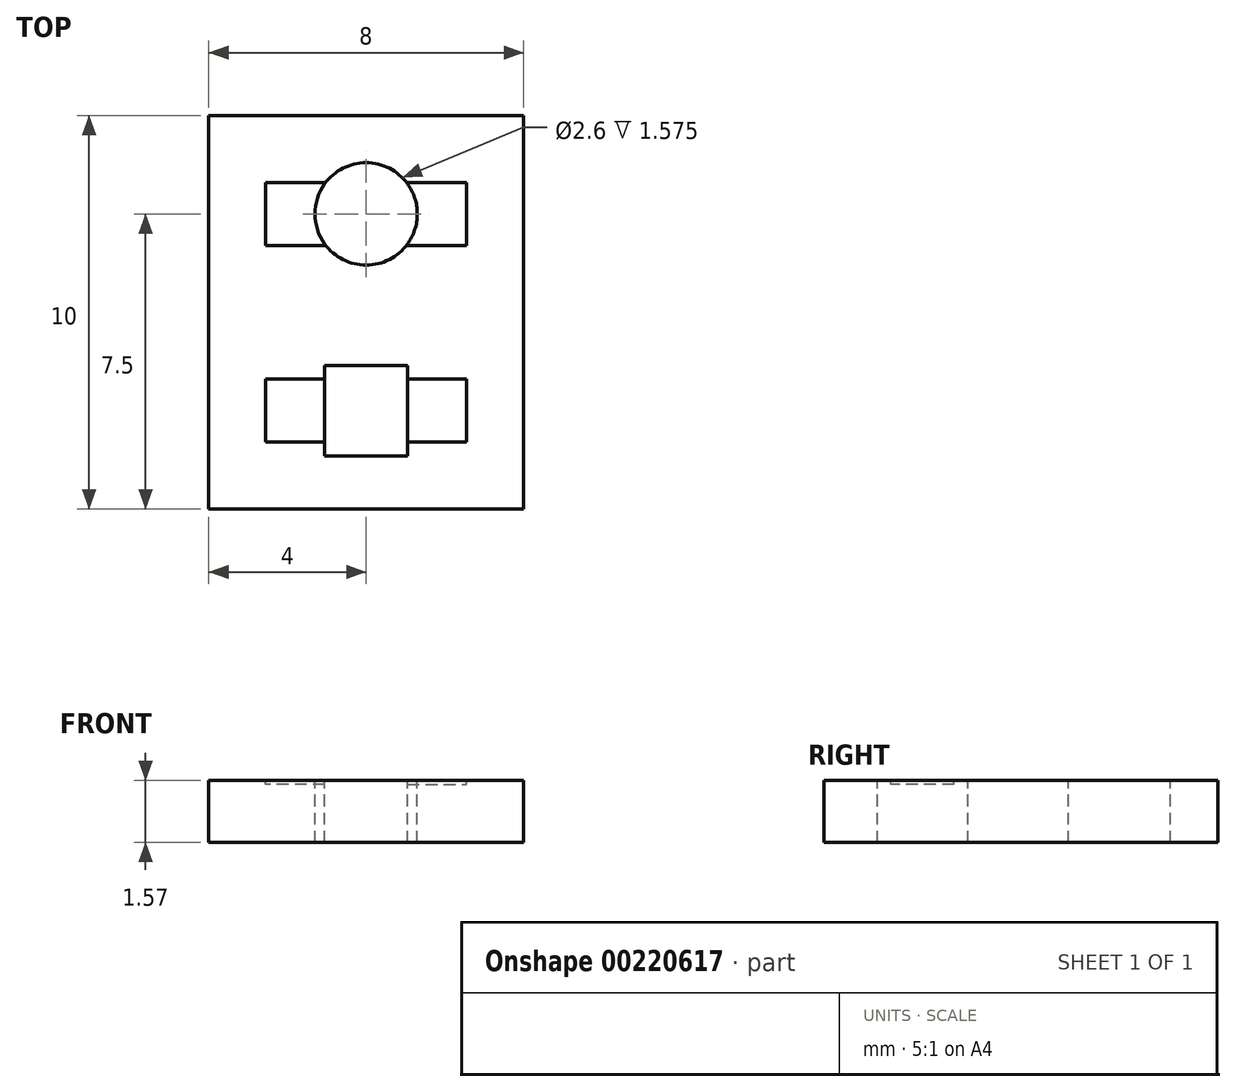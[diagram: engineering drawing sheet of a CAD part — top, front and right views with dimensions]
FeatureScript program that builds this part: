
annotation { "Feature Type Name" : "Feature", "Feature Type Description" : "" }
export const myFeature = defineFeature(function(context is Context, id is Id, definition is map)
    precondition{}
    {
        {
            var Q0;
            Q0=qCreatedBy(makeId("Top.planeOp"),FACE);
            var sketch = newSketch(context, id + "F0", { "sketchPlane" : qUnion([Q0])});
            skLineSegment(sketch, "E0.bottom", {"start": v(4, 2.5) * mm, "end": v(-4, 2.5) * mm});
            skLineSegment(sketch, "E0.top", {"start": v(4, -2.5) * mm, "end": v(-4, -2.5) * mm});
            skLineSegment(sketch, "E0.left", {"start": v(4, 2.5) * mm, "end": v(4, -2.5) * mm});
            skLineSegment(sketch, "E0.right", {"start": v(-4, 2.5) * mm, "end": v(-4, -2.5) * mm});
            skPoint(sketch, "E0.middle", {"position": v(0, 0) * mm});
            skLineSegment(sketch, "E1.bottom", {"start": v(1.05, 1.15) * mm, "end": v(-1.05, 1.15) * mm});
            skLineSegment(sketch, "E1.top", {"start": v(1.05, -1.15) * mm, "end": v(-1.05, -1.15) * mm});
            skLineSegment(sketch, "E1.left", {"start": v(1.05, 1.15) * mm, "end": v(1.05, -1.15) * mm});
            skLineSegment(sketch, "E1.right", {"start": v(-1.05, 1.15) * mm, "end": v(-1.05, -1.15) * mm});
            skLineSegment(sketch, "E2.bottom", {"start": v(-1.05, 0.8) * mm, "end": v(-2.55, 0.8) * mm});
            skLineSegment(sketch, "E2.top", {"start": v(-1.05, -0.8) * mm, "end": v(-2.55, -0.8) * mm});
            skLineSegment(sketch, "E2.left", {"start": v(-1.05, 0.8) * mm, "end": v(-1.05, -0.8) * mm});
            skLineSegment(sketch, "E2.right", {"start": v(-2.55, 0.8) * mm, "end": v(-2.55, -0.8) * mm});
            skLineSegment(sketch, "E3.bottom", {"start": v(1.05, -0.8) * mm, "end": v(2.55, -0.8) * mm});
            skLineSegment(sketch, "E3.top", {"start": v(1.05, 0.8) * mm, "end": v(2.55, 0.8) * mm});
            skLineSegment(sketch, "E3.left", {"start": v(1.05, 0.8) * mm, "end": v(1.05, -0.8) * mm});
            skLineSegment(sketch, "E3.right", {"start": v(2.55, 0.8) * mm, "end": v(2.55, -0.8) * mm});
            skLineSegment(sketch, "E4", {"start": v(-1.05, 0) * mm, "end": v(0, 0) * mm, "construction": true});
            skLineSegment(sketch, "E5", {"start": v(0, 0) * mm, "end": v(1.05, 0) * mm, "construction": true});
            skLineSegment(sketch, "E6", {"start": v(-1.8, 0.8) * mm, "end": v(-1.8, -0.8) * mm, "construction": true});
            skSolve(sketch);
        }
        {
            var Q0;
            Q0 = qSketchRegion(id + "F0", true);
            var Q1;
            Q1=makeQuery(id+"F0.imprint","IMPRINT",FACE,{"disambiguationData":[TD([[makeQuery(id+"F0.imprint","IMPRINT",EDGE,{"derivedFrom":sQuery(id+"F0.wireOp",EDGE,"E2.bottom")}),1.0]])]});
            var Q2;
            Q2=makeQuery(id+"F0.imprint","IMPRINT",FACE,{"disambiguationData":[TD([[makeQuery(id+"F0.imprint","IMPRINT",EDGE,{"derivedFrom":sQuery(id+"F0.wireOp",EDGE,"E3.bottom")}),1.0]])]});
            extrude(context, id + "F1", {"entities" : qUnion([Q0, Q1, Q2]), "oppositeDirection" : true, "depth" : 1.57 * mm});
        }
        {
            var Q0;
            Q0=makeQuery(id+"F0.imprint","IMPRINT",FACE,{"disambiguationData":[TD([[makeQuery(id+"F0.imprint","IMPRINT",EDGE,{"derivedFrom":sQuery(id+"F0.wireOp",EDGE,"E2.bottom")}),1.0]])]});
            var Q1;
            Q1=makeQuery(id+"F0.imprint","IMPRINT",FACE,{"disambiguationData":[TD([[makeQuery(id+"F0.imprint","IMPRINT",EDGE,{"derivedFrom":sQuery(id+"F0.wireOp",EDGE,"E3.bottom")}),1.0]])]});
            extrude(context, id + "F2", {"entities" : qUnion([Q0, Q1]), "operationType" : NewBodyOperationType.REMOVE, "oppositeDirection" : true, "depth" : .1 * mm});
        }
        {
            var Q0;
            Q0=makeQuery(id+"F1.opExtrude","SWEPT_FACE",FACE,{"disambiguationData":[OSD([sQuery(id+"F0.wireOp",EDGE,"E0.bottom")])]});
            extrude(context, id + "F3", {"entities" : qUnion([Q0]), "operationType" : NewBodyOperationType.ADD, "depth" : 5 * mm});
        }
        {
            var Q0;
            {var subQ0=sQuery(id+"F0.wireOp",EDGE,"E0.bottom");Q0=makeQuery(id+"F3.boolean.opBoolean","MERGE",FACE,{"derivedFrom":[makeQuery(id+"F1.opExtrude","CAP_FACE",FACE,{"disambiguationData":[OSD([subQ0,sQuery(id+"F0.wireOp",EDGE,"E0.top"),sQuery(id+"F0.wireOp",EDGE,"E0.left"),sQuery(id+"F0.wireOp",EDGE,"E0.right"),sQuery(id+"F0.wireOp",EDGE,"E1.bottom"),sQuery(id+"F0.wireOp",EDGE,"E1.top"),sQuery(id+"F0.wireOp",EDGE,"E1.left"),sQuery(id+"F0.wireOp",EDGE,"E1.right"),sQuery(id+"F0.wireOp",EDGE,"E2.left"),sQuery(id+"F0.wireOp",EDGE,"E3.left")])],"isStart":true}),makeQuery(id+"F3.opExtrude","SWEPT_FACE",FACE,{"disambiguationData":[OSD([subQ0]),TDD([makeQuery(id+"F1.opExtrude","CAP_EDGE",EDGE,{"disambiguationData":[OSD([subQ0])],"isStart":true})])]})]});}
            var sketch = newSketch(context, id + "F4", { "sketchPlane" : qUnion([Q0])});
            skLineSegment(sketch, "E7", {"start": v(0, 0) * mm, "end": v(0, 5) * mm, "construction": true});
            skCircle(sketch, "E8", {"center": v(0, 5) * mm, "radius": 1.3 * mm});
            skLineSegment(sketch, "E9", {"start": v(-4, 7.5) * mm, "end": v(0, 5) * mm, "construction": true});
            skLineSegment(sketch, "E10", {"start": v(-4, 2.5) * mm, "end": v(0, 5) * mm, "construction": true});
            skLineSegment(sketch, "E11.bottom", {"start": v(2.55, 5.8) * mm, "end": v(1.05, 5.8) * mm});
            skLineSegment(sketch, "E11.top", {"start": v(2.55, 4.2) * mm, "end": v(1.05, 4.2) * mm});
            skLineSegment(sketch, "E11.left", {"start": v(2.55, 5.8) * mm, "end": v(2.55, 4.2) * mm});
            skLineSegment(sketch, "E11.right", {"start": v(1.05, 5.8) * mm, "end": v(1.05, 4.2) * mm});
            skLineSegment(sketch, "E12.bottom", {"start": v(-2.55, 5.8) * mm, "end": v(-1.05, 5.8) * mm});
            skLineSegment(sketch, "E12.top", {"start": v(-2.55, 4.2) * mm, "end": v(-1.05, 4.2) * mm});
            skLineSegment(sketch, "E12.left", {"start": v(-2.55, 5.8) * mm, "end": v(-2.55, 4.2) * mm});
            skLineSegment(sketch, "E12.right", {"start": v(-1.05, 5.8) * mm, "end": v(-1.05, 4.2) * mm});
            skLineSegment(sketch, "E13", {"start": v(0, 5) * mm, "end": v(-1.05, 5) * mm});
            skLineSegment(sketch, "E14", {"start": v(0, 5) * mm, "end": v(1.05, 5) * mm});
            skSolve(sketch);
        }
        {
            var Q0;
            {var subQ0=sQuery(id+"F4.wireOp",EDGE,"E13");Q0=makeQuery(id+"F4.imprint","IMPRINT",FACE,{"disambiguationData":[TD([[makeQuery(id+"F4.imprint","IMPRINT",EDGE,{"derivedFrom":subQ0}),1.0]])]});}
            var Q1;
            {var subQ0=sQuery(id+"F4.wireOp",EDGE,"E12.right");var subQ1=sQuery(id+"F4.wireOp",EDGE,"E8");var subQ2=makeQuery(id+"F4.imprint","INTERSECT",VERTEX,{"disambiguationData":[OD(0.0)],"derivedFrom":[subQ1,subQ0]});Q1=makeQuery(id+"F4.imprint","IMPRINT",FACE,{"disambiguationData":[TD([[makeQuery(id+"F4.imprint","IMPRINT",EDGE,{"disambiguationData":[TD([[subQ2,-1.0]])],"derivedFrom":subQ1}),1.0]])]});}
            var Q2;
            {var subQ0=sQuery(id+"F4.wireOp",EDGE,"E13");Q2=makeQuery(id+"F4.imprint","IMPRINT",FACE,{"disambiguationData":[TD([[makeQuery(id+"F4.imprint","IMPRINT",EDGE,{"derivedFrom":subQ0}),-1.0]])]});}
            var Q3;
            {var subQ0=sQuery(id+"F4.wireOp",EDGE,"E11.right");var subQ1=sQuery(id+"F4.wireOp",EDGE,"E8");var subQ2=makeQuery(id+"F4.imprint","INTERSECT",VERTEX,{"disambiguationData":[OD(0.0)],"derivedFrom":[subQ1,subQ0]});Q3=makeQuery(id+"F4.imprint","IMPRINT",FACE,{"disambiguationData":[TD([[makeQuery(id+"F4.imprint","IMPRINT",EDGE,{"disambiguationData":[TD([[subQ2,1.0]])],"derivedFrom":subQ1}),1.0]])]});}
            var Q4;
            Q4=sQuery(id+"F4.wireOp",EDGE,"E8");
            extrude(context, id + "F5", {"entities" : qUnion([Q0, Q1, Q2, Q3]), "operationType" : NewBodyOperationType.REMOVE, "surfaceEntities" : qUnion([Q4]), "oppositeDirection" : true, "depth" : 25 * mm});
        }
        {
            var Q0;
            {var subQ1=sQuery(id+"F4.wireOp",EDGE,"E12.bottom");Q0=makeQuery(id+"F4.imprint","IMPRINT",FACE,{"disambiguationData":[TD([[makeQuery(id+"F4.imprint","IMPRINT",EDGE,{"derivedFrom":subQ1}),-1.0]])]});}
            var Q1;
            {var subQ4=sQuery(id+"F4.wireOp",EDGE,"E11.bottom");Q1=makeQuery(id+"F4.imprint","IMPRINT",FACE,{"disambiguationData":[TD([[makeQuery(id+"F4.imprint","IMPRINT",EDGE,{"derivedFrom":subQ4}),1.0]])]});}
            extrude(context, id + "F6", {"entities" : qUnion([Q0, Q1]), "operationType" : NewBodyOperationType.REMOVE, "oppositeDirection" : true, "depth" : 0.01 * mm});
        }
    });
